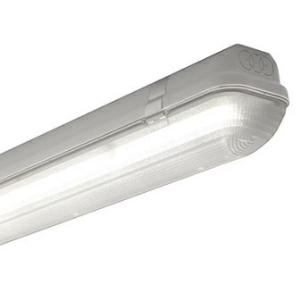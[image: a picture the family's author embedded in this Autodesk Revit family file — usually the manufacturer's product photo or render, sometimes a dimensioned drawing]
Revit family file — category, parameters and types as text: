
# Revit family: 3f_filippi_-_3f_linda_hq_3f_filippi_-_58867_-_3f_linda_led_1x12w-940_l660
name_source: partatom
category: Lighting Fixtures
units: mm (PartAtom-declared; Revit-internal decimal feet)

## family parameters
Cut with Voids When Loaded = No
Host = Face
Light Source = No
Part Type = Normal
Room Calculation Point = No
Round Connector Dimension = Use Diameter
Shared = No

## types (1)
- 3F Filippi - 3F Linda HQ (1 x LED, 1575 lm, 14 W, 4000 K)
    Apparent Load = 14 VA
    Approval mark = CE
    CIE Flux Codes = 44 77 94 97 100
    Color Rendering = 90
    Color Temperature = 4000 K
    Control Gear = Electronic ballast
    Default Elevation = 1800 mm
    Description = ILLUMINOTECHNICAL
Luminous efficiency 100% (DLOR 97%, ULOR 3%).
Initial luminous flux of the luminaire 1575 lm.
Controlled symmetric distribution.
Installation Interdistance Transv.D = 1.77 x hu - Long.D = 1.17 x hu.
Tabular UGR (CIE 117 - 4H-8H; S=0.25H; 70/50/20): RUG 20.9 - 21.7.
Beam angle: 109° - 64°.
Luminous efficacy 113 lm/W.
Lifetime (L93/B10): 30000 h. (tq+25°C)
Lifetime (L90/B10): 50000 h. (tq+25°C)
Lifetime (L85/B10): 80000 h. (tq+25°C)
Lifetime (L80/B10): 100000 h. (tq+25°C)
Lifetime (L85/B10): 50000 h. (tq+35°C)
Sudden decreased luminous flux after 50000 hours: 0% (C0).
Photobiological safety in compliance with IEC/TR 62778: RG0 risk exempt, (IEC 62471).
In compliance with IEC/EN 62722-2-1 - IEC/EN 62717 standards.

SOURCE
Linear LED module 12W/940.
Energy efficiency class (UE 2019/2020 - UE 2019/2015): E.
CIE 13.3 Colour rendering index: CRI >90 (R9 >50%).
IES TM-30 Fidelity Index: Rf = 92 Rg = 101.
CCT nominal colour temperature 4000 K.
Colour initial tolerance (MacAdam): SDCM 3.

MECHANICAL
Self-extinguishing V2 polycarbonate housing, injection moulded, RAL 7035 grey.
Ecologic anti-aging injected sealing gasket.
Diffuser in self-extinguishing V2 polycarbonate, photo-engraved interior, UV stabilised, injection moulded with smooth outer surface, tamper-proof opening.
Gear-holder reflector in hot-dip galvanised steel, painted with white polyester base.
Snug fit safety snap-lock clips for diffuser mounting in stainless steel, screwdriver opening.
Fixing brackets in stainless steel.
Possibility for technicians to access the interior of the luminaire.
Luminaire with limited surface temperature. - D - (EN 60598-2-24)
Dimensions: 660x100 mm, height 100 mm. Weight 1.2 kg.
IP66 protection degree.
Mechanical strength to impacts IK10 (20 joule).
Glow-wire test resistance 850°C.

ELECTRICAL
Halogen Free electronic wiring 230V-50/60Hz, power factor 0.95, THD <25%, constant output current, SELV, class I, 1 driver.
Power of the luminaire 14 W.
ENEC - CE.
SAFE FLICKER: PstLM=<1 and SVM=<0.4 (IEC TR 61547-1 and IEC TR 63158), to ensure a more comfortable and safe light.
Luminaire compliant with EN 60598-2-22 for power supply from a centralised emergency system CPSS (Central Power Supply System), not incorporated in the luminaire - high risk areas excluded. The default power and flux are 100% in AC and 100% in DC.
Ambient temperature from -20°C to +35°C.
Temperature class T6 max 85°C.
Relative humidity UR: <85%.

INSTALLATION
Ceiling / Suspended / Wall.
All accessories dedicated to this product are available on the Catalog and on our website www.3F-Filippi.com.

APPLICATIONS
Suitable product for food production plants (HACCP), IFS (Food Version 6), BRC (GSFS Food Version 7).
Dry, dusty indoor environments, subject to occasional water splashes.
Virtually shatterproof polycarbonate compatibly with the fumes / atmospheres that compromise the elasticity of plastic materials.
Not suitable for installation on surfaces subject to important vibrations, exposed to weather conditions, on ropes or poles.
Suitable for illumination of public car parks and parking grounds referred to DIN 67528:2018-04.

WARNING
Fixture not suitable for cold stores with an ambient temperature <0°C and/or relative humidity >85%.
Luminaire designed for disposal/recycling at end-of-life.
Replaceable (LED only) light source by a professional. Replaceable control gear by a professional.
    Height = 100 mm  [stored 0.328084 ft]
    Lamp = 1 x LED
    Lamp Light Flux = 1575 lm
    Lamp Power = 14 W
    Lamp count = 1
    Length = 660 mm
    Lifetime = 50000 h
    Luminous efficacy = 113 lm/W
    Manufacturer = 3F Filippi
    ModVariant = No
    Model = 3F Filippi - 58867 - 3F Linda LED 1x12W-940 L660
    Mounting Place = Ceiling
    Mounting Type = Pendant
    Number of Poles = 1
    OnlyDefault = Yes
    Power Factor = 1
    Product Name = 3F Filippi - 3F Linda HQ
    Product group = pendant luminaire
    ProductGroupID = 9
    Protection Class = Protection class I
    Protection Degree = IP 66
    RLX_Detail_Level = 1
    RLX_Emergency_Light_Flux = 0 lm
    RLX_Emergency_Type = 0
    RLX_Emergency_Type_DB = No
    RlxData = <blob elided: 69545 chars, md5=08df1543>
    Socket = socket
    Standby Power = 0 W
    System Light Flux = 1575 lm
    System Power = 14 W
    Type Comments = Product without accessories
    Type Image = 3ffilippi_3f_linda_led_1x.jpg
    URL = http://relux.com
    VarID = ---
    Voltage = 0 V
    Weight = 0.00 kg
    Width = 100 mm  [stored 0.328084 ft]

note: [stored X ft] marks values corroborated as IEEE doubles in the binary element streams (Revit-internal decimal feet)

## geometry (parser evidence)
native form markers: Blend x4, Sweep x9
no freeform markers — native parametric forms only
